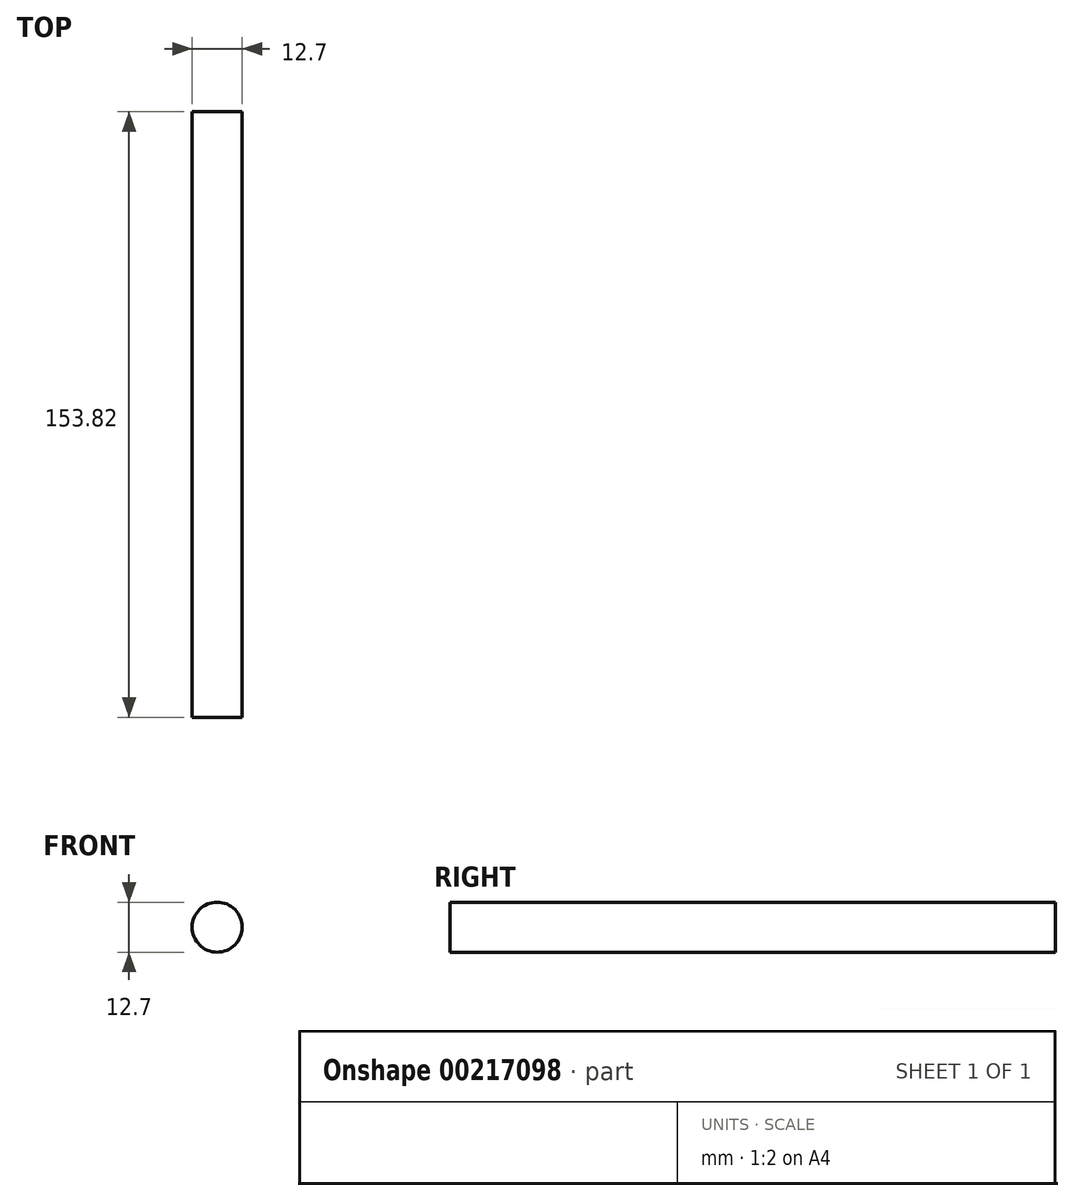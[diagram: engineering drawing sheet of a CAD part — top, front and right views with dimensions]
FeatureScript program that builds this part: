
annotation { "Feature Type Name" : "Feature", "Feature Type Description" : "" }
export const myFeature = defineFeature(function(context is Context, id is Id, definition is map)
    precondition{}
    {
        {
            var Q0;
            Q0=qCreatedBy(makeId("Front.planeOp"),FACE);
            var sketch = newSketch(context, id + "F0", { "sketchPlane" : qUnion([Q0])});
            skCircle(sketch, "E0", {"center": v(0, 0) * mm, "radius": 6.35 * mm});
            skSolve(sketch);
        }
        {
            var Q0;
            Q0 = qSketchRegion(id + "F0", true);
            extrude(context, id + "F1", {"entities" : qUnion([Q0]), "depth" : 153.82 * mm});
        }
    });
